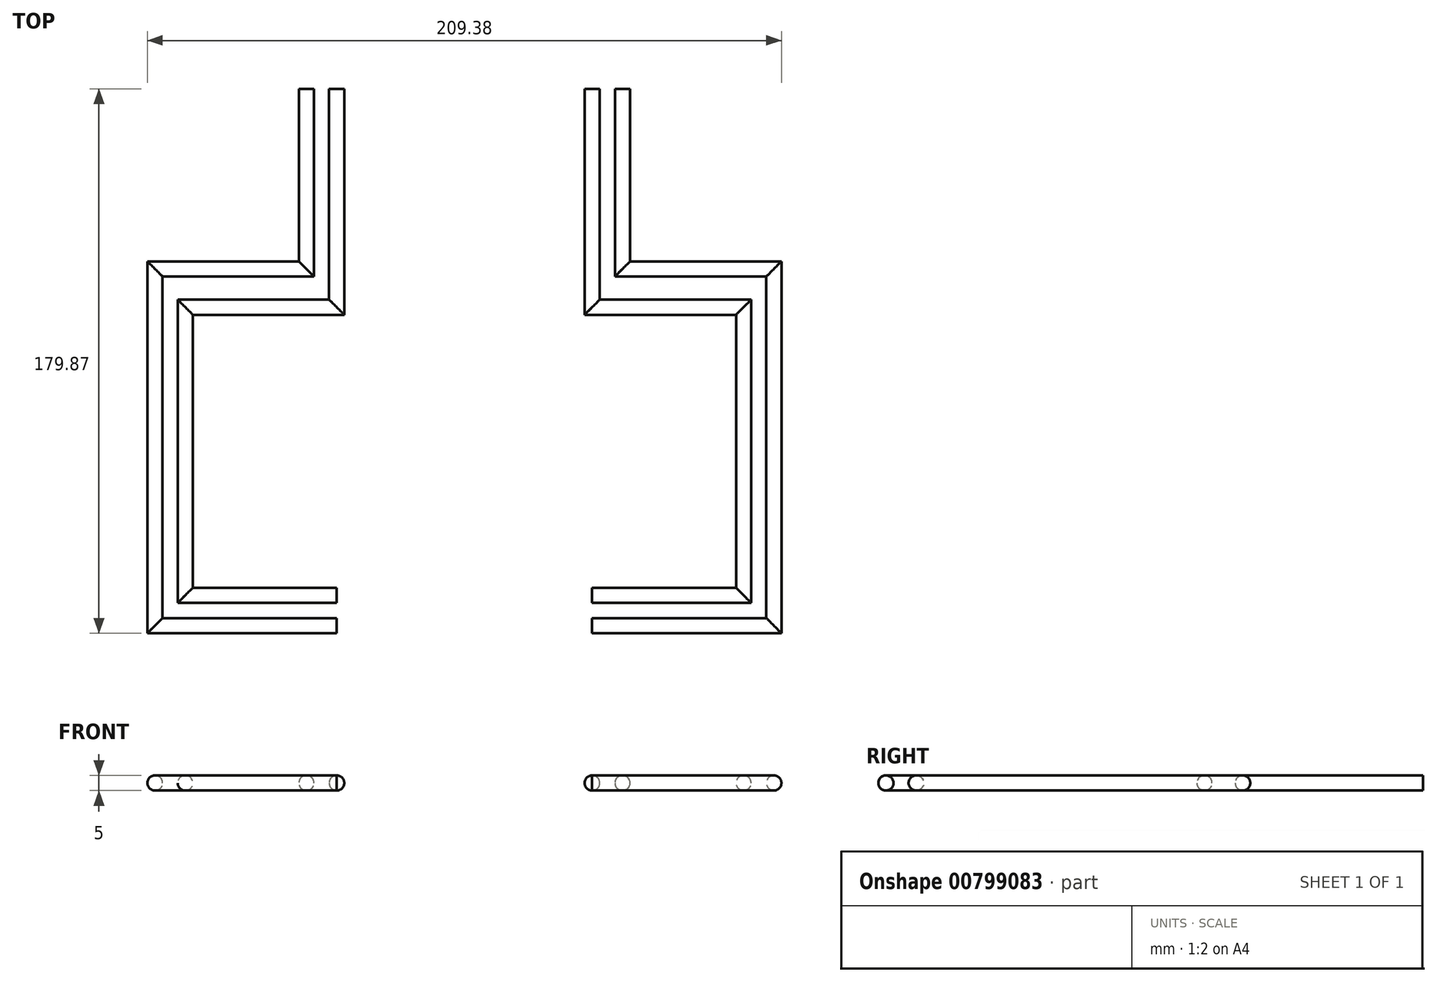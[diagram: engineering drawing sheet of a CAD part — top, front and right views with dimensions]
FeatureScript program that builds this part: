
annotation { "Feature Type Name" : "Feature", "Feature Type Description" : "" }
export const myFeature = defineFeature(function(context is Context, id is Id, definition is map)
    precondition{}
    {
        {
            var Q0;
            Q0=qCreatedBy(makeId("Top.planeOp"),FACE);
            var sketch = newSketch(context, id + "F0", { "sketchPlane" : qUnion([Q0])});
            skLineSegment(sketch, "E0", {"start": v(-29.96, 0) * mm, "end": v(-29.96, -59.54) * mm});
            skLineSegment(sketch, "E1", {"start": v(74.42, 0) * mm, "end": v(74.42, -59.54) * mm});
            skLineSegment(sketch, "E2", {"start": v(74.42, -59.54) * mm, "end": v(124.42, -59.54) * mm});
            skLineSegment(sketch, "E3", {"start": v(124.42, -59.54) * mm, "end": v(124.42, -177.37) * mm});
            skLineSegment(sketch, "E4", {"start": v(124.42, -177.37) * mm, "end": v(64.42, -177.37) * mm});
            skLineSegment(sketch, "E5", {"start": v(-29.96, -59.54) * mm, "end": v(-79.96, -59.54) * mm});
            skLineSegment(sketch, "E6", {"start": v(-79.96, -59.54) * mm, "end": v(-79.96, -177.37) * mm});
            skLineSegment(sketch, "E7", {"start": v(-79.96, -177.37) * mm, "end": v(-19.96, -177.37) * mm});
            skLineSegment(sketch, "E8", {"start": v(-19.96, 0) * mm, "end": v(-19.96, -72.16) * mm});
            skLineSegment(sketch, "E9", {"start": v(-19.96, -72.16) * mm, "end": v(-69.96, -72.16) * mm});
            skLineSegment(sketch, "E10", {"start": v(-69.96, -72.16) * mm, "end": v(-69.96, -167.37) * mm});
            skLineSegment(sketch, "E11", {"start": v(-69.96, -167.37) * mm, "end": v(-19.96, -167.37) * mm});
            skLineSegment(sketch, "E12", {"start": v(64.42, -167.37) * mm, "end": v(114.42, -167.37) * mm});
            skLineSegment(sketch, "E13", {"start": v(114.42, -167.37) * mm, "end": v(114.42, -72.16) * mm});
            skLineSegment(sketch, "E14", {"start": v(114.42, -72.16) * mm, "end": v(64.42, -72.16) * mm});
            skLineSegment(sketch, "E15", {"start": v(64.42, -72.16) * mm, "end": v(64.42, 0) * mm});
            skLineSegment(sketch, "E16", {"start": v(-29.96, -59.54) * mm, "end": v(-19.96, -59.54) * mm});
            skLineSegment(sketch, "E17", {"start": v(64.42, -59.54) * mm, "end": v(74.42, -59.54) * mm});
            skLineSegment(sketch, "E18", {"start": v(-19.96, -59.54) * mm, "end": v(22.23, -59.54) * mm});
            skLineSegment(sketch, "E19", {"start": v(22.23, -59.54) * mm, "end": v(64.42, -59.54) * mm});
            skSolve(sketch);
        }
        {
            var Q0;
            Q0=qCreatedBy(makeId("Front.planeOp"),FACE);
            var sketch = newSketch(context, id + "F1", { "sketchPlane" : qUnion([Q0])});
            skCircle(sketch, "E20", {"center": v(-29.96, 0) * mm, "radius": 2.5 * mm});
            skCircle(sketch, "E21", {"center": v(-19.96, 0) * mm, "radius": 2.5 * mm});
            skCircle(sketch, "E22", {"center": v(64.42, 0) * mm, "radius": 2.5 * mm});
            skCircle(sketch, "E23", {"center": v(74.42, 0) * mm, "radius": 2.5 * mm});
            skSolve(sketch);
        }
        {
            var Q0;
            Q0=makeQuery(id+"F1.imprint","IMPRINT",FACE,{"disambiguationData":[TD([[makeQuery(id+"F1.imprint","IMPRINT",EDGE,{"derivedFrom":sQuery(id+"F1.wireOp",EDGE,"E20")}),1.0]])]});
            var Q1;
            Q1=sQuery(id+"F0.wireOp",EDGE,"E0");
            var Q2;
            Q2=sQuery(id+"F0.wireOp",EDGE,"E5");
            var Q3;
            Q3=sQuery(id+"F0.wireOp",EDGE,"E6");
            var Q4;
            Q4=sQuery(id+"F0.wireOp",EDGE,"E7");
            sweep(context, id + "F2", {"profiles" : qUnion([Q0]), "path" : qUnion([Q1, Q2, Q3, Q4])});
        }
        {
            var Q0;
            Q0=makeQuery(id+"F1.imprint","IMPRINT",FACE,{"disambiguationData":[TD([[makeQuery(id+"F1.imprint","IMPRINT",EDGE,{"derivedFrom":sQuery(id+"F1.wireOp",EDGE,"E21")}),1.0]])]});
            var Q1;
            Q1=sQuery(id+"F0.wireOp",EDGE,"E8");
            var Q2;
            Q2=sQuery(id+"F0.wireOp",EDGE,"E9");
            var Q3;
            Q3=sQuery(id+"F0.wireOp",EDGE,"E10");
            var Q4;
            Q4=sQuery(id+"F0.wireOp",EDGE,"E11");
            sweep(context, id + "F3", {"profiles" : qUnion([Q0]), "path" : qUnion([Q1, Q2, Q3, Q4])});
        }
        {
            var Q0;
            Q0=makeQuery(id+"F1.imprint","IMPRINT",FACE,{"disambiguationData":[TD([[makeQuery(id+"F1.imprint","IMPRINT",EDGE,{"derivedFrom":sQuery(id+"F1.wireOp",EDGE,"E22")}),1.0]])]});
            var Q1;
            Q1=sQuery(id+"F0.wireOp",EDGE,"E15");
            var Q2;
            Q2=sQuery(id+"F0.wireOp",EDGE,"E14");
            var Q3;
            Q3=sQuery(id+"F0.wireOp",EDGE,"E13");
            var Q4;
            Q4=sQuery(id+"F0.wireOp",EDGE,"E12");
            sweep(context, id + "F4", {"profiles" : qUnion([Q0]), "path" : qUnion([Q1, Q2, Q3, Q4])});
        }
        {
            var Q0;
            Q0=makeQuery(id+"F1.imprint","IMPRINT",FACE,{"disambiguationData":[TD([[makeQuery(id+"F1.imprint","IMPRINT",EDGE,{"derivedFrom":sQuery(id+"F1.wireOp",EDGE,"E23")}),1.0]])]});
            var Q1;
            Q1=sQuery(id+"F0.wireOp",EDGE,"E1");
            var Q2;
            Q2=sQuery(id+"F0.wireOp",EDGE,"E2");
            var Q3;
            Q3=sQuery(id+"F0.wireOp",EDGE,"E3");
            var Q4;
            Q4=sQuery(id+"F0.wireOp",EDGE,"E4");
            sweep(context, id + "F5", {"profiles" : qUnion([Q0]), "path" : qUnion([Q1, Q2, Q3, Q4])});
        }
    });
